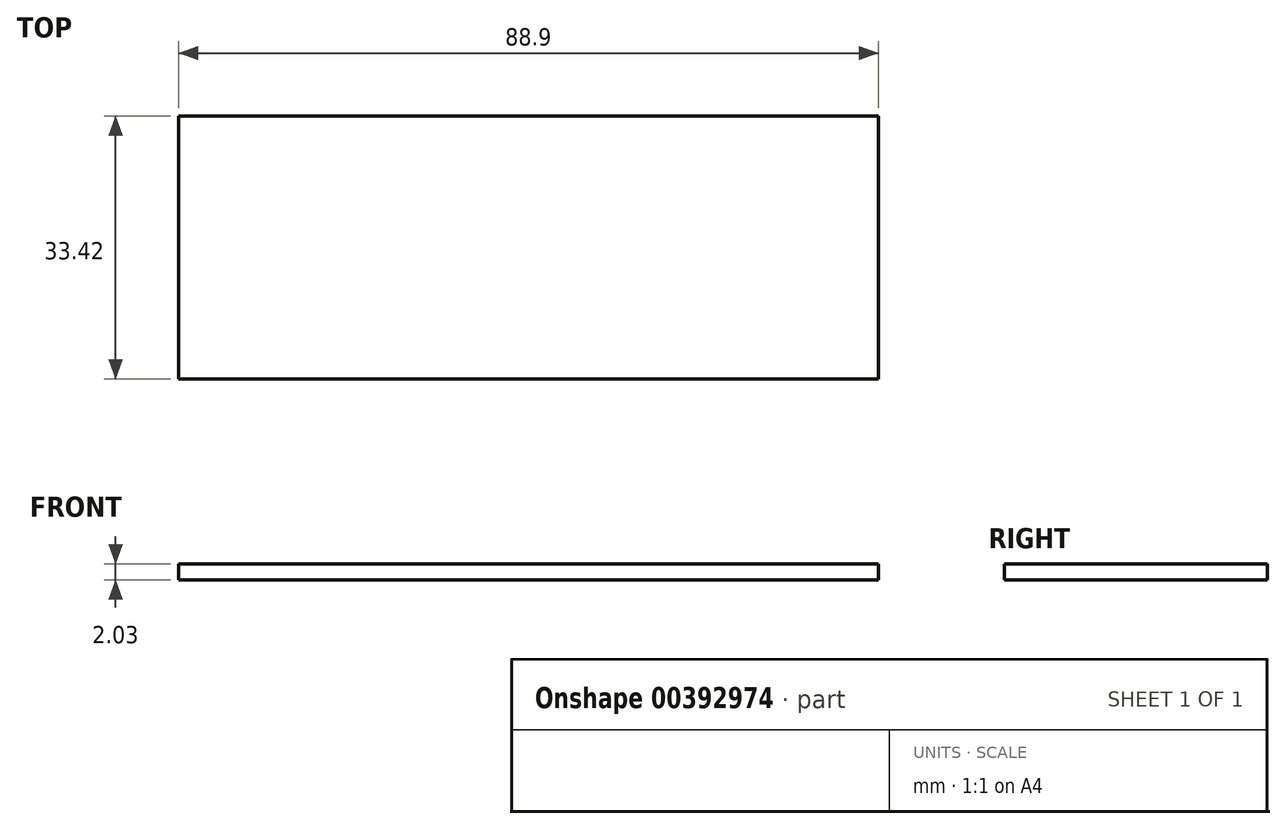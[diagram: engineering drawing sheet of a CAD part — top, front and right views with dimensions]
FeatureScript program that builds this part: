
annotation { "Feature Type Name" : "Feature", "Feature Type Description" : "" }
export const myFeature = defineFeature(function(context is Context, id is Id, definition is map)
    precondition{}
    {
        {
            var Q0;
            Q0=qCreatedBy(makeId("Top.planeOp"),FACE);
            var sketch = newSketch(context, id + "F0", { "sketchPlane" : qUnion([Q0])});
            skLineSegment(sketch, "E0.bottom", {"start": v(-44.45, 16.71) * mm, "end": v(44.45, 16.71) * mm});
            skLineSegment(sketch, "E0.top", {"start": v(-44.45, -16.71) * mm, "end": v(44.45, -16.71) * mm});
            skLineSegment(sketch, "E0.left", {"start": v(-44.45, 16.71) * mm, "end": v(-44.45, -16.71) * mm});
            skLineSegment(sketch, "E0.right", {"start": v(44.45, 16.71) * mm, "end": v(44.45, -16.71) * mm});
            skPoint(sketch, "E0.middle", {"position": v(0, 0) * mm});
            skSolve(sketch);
        }
        {
            var Q0;
            Q0=qSketchRegion(id+"F0",true);
            extrude(context, id + "F1", {"entities" : qUnion([Q0]), "depth" : 2.03 * mm});
        }
    });
